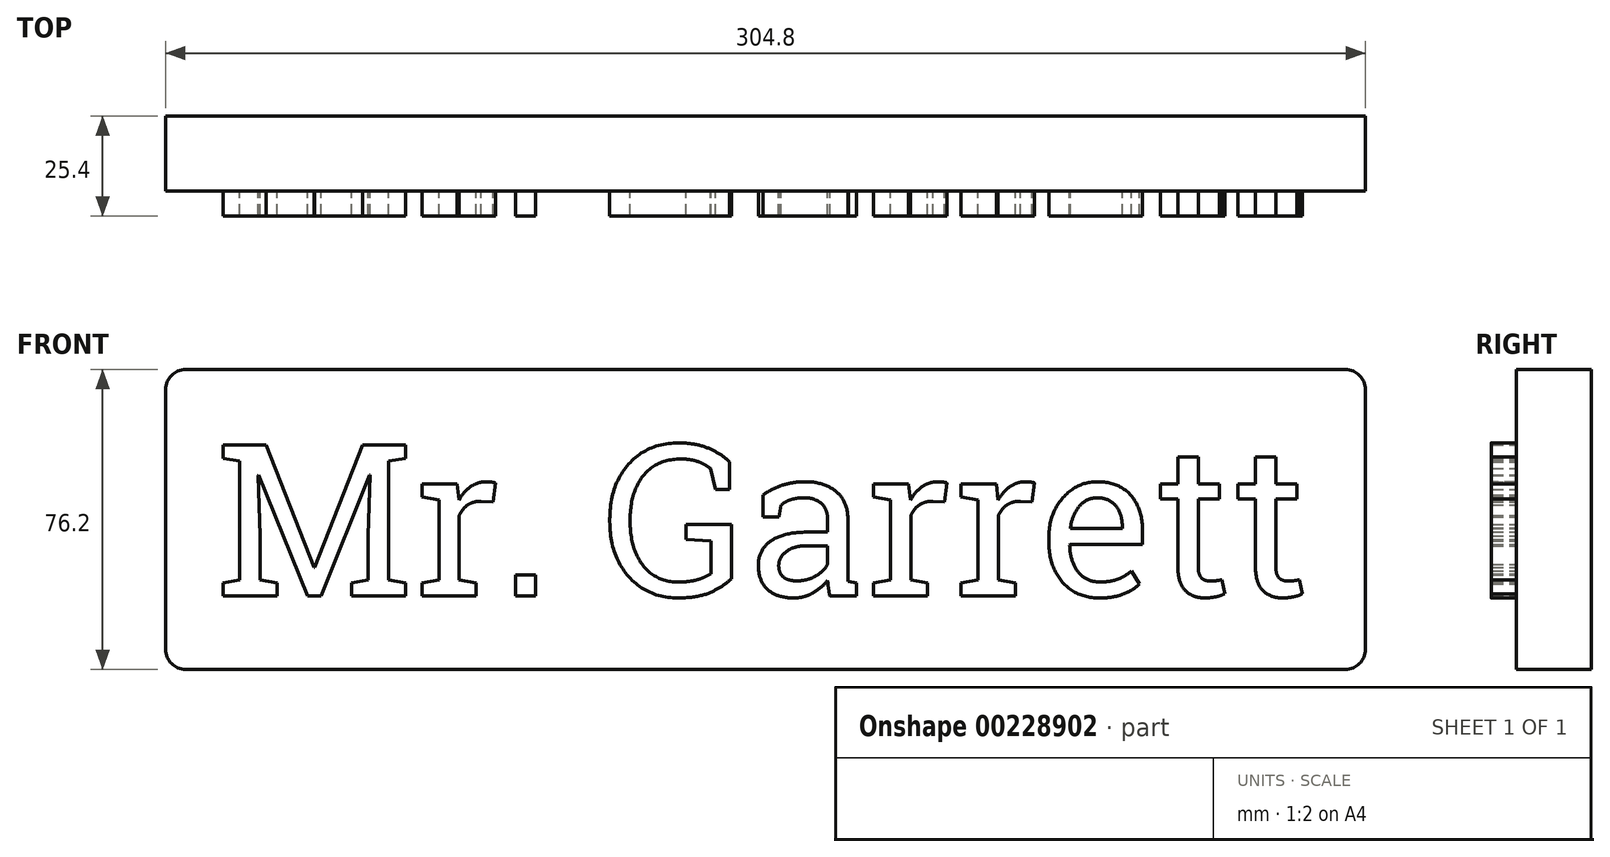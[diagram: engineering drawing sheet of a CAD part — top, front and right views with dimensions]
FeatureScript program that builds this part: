
annotation { "Feature Type Name" : "Feature", "Feature Type Description" : "" }
export const myFeature = defineFeature(function(context is Context, id is Id, definition is map)
    precondition{}
    {
        {
            var Q0;
            Q0=qCreatedBy(makeId("Front.planeOp"),FACE);
            var sketch = newSketch(context, id + "F0", { "sketchPlane" : qUnion([Q0])});
            skLineSegment(sketch, "E0.bottom", {"start": v(-152.4, 38.1) * mm, "end": v(152.4, 38.1) * mm});
            skLineSegment(sketch, "E0.top", {"start": v(-152.4, -38.1) * mm, "end": v(152.4, -38.1) * mm});
            skLineSegment(sketch, "E0.left", {"start": v(-152.4, 38.1) * mm, "end": v(-152.4, -38.1) * mm});
            skLineSegment(sketch, "E0.right", {"start": v(152.4, 38.1) * mm, "end": v(152.4, -38.1) * mm});
            skPoint(sketch, "E0.middle", {"position": v(0, 0) * mm});
            skSolve(sketch);
        }
        {
            var Q0;
            Q0=makeQuery(id+"F0.imprint","IMPRINT",FACE,{"disambiguationData":[TD([[makeQuery(id+"F0.imprint","IMPRINT",EDGE,{"derivedFrom":sQuery(id+"F0.wireOp",EDGE,"E0.bottom")}),-1.0]])]});
            extrude(context, id + "F1", {"entities" : qUnion([Q0]), "depth" : 19.05 * mm});
        }
        {
            var Q0;
            Q0=makeQuery(id+"F1.opExtrude","CAP_FACE",FACE,{"disambiguationData":[OSD([sQuery(id+"F0.wireOp",EDGE,"E0.bottom"),sQuery(id+"F0.wireOp",EDGE,"E0.top"),sQuery(id+"F0.wireOp",EDGE,"E0.left"),sQuery(id+"F0.wireOp",EDGE,"E0.right")])],"isStart":false});
            var sketch = newSketch(context, id + "F2", { "sketchPlane" : qUnion([Q0])});
            skText(sketch, "E1", { "text": "Mr. Garrett", "fontName": "RobotoSlab-Regular.ttf"});
            const initialGuessF2  = {"E1": [-0.1397, -0.01938, 1, 0, 0.03876]};
            skSetInitialGuess(sketch, initialGuessF2);
            skSolve(sketch);
        }
        {
            var Q0;
            Q0 = qSketchRegion(id + "F2", true);
            extrude(context, id + "F3", {"entities" : qUnion([Q0]), "operationType" : NewBodyOperationType.ADD, "depth" : 6.35 * mm});
        }
        {
            var Q0;
            Q0=makeQuery(id+"F1.opExtrude","SWEPT_EDGE",EDGE,{"disambiguationData":[OSD([sQuery(id+"F0.wireOp",EDGE,"E0.bottom"),sQuery(id+"F0.wireOp",EDGE,"E0.left")])]});
            var Q1;
            Q1=makeQuery(id+"F1.opExtrude","SWEPT_EDGE",EDGE,{"disambiguationData":[OSD([sQuery(id+"F0.wireOp",EDGE,"E0.bottom"),sQuery(id+"F0.wireOp",EDGE,"E0.right")])]});
            var Q2;
            Q2=makeQuery(id+"F1.opExtrude","SWEPT_EDGE",EDGE,{"disambiguationData":[OSD([sQuery(id+"F0.wireOp",EDGE,"E0.top"),sQuery(id+"F0.wireOp",EDGE,"E0.right")])]});
            var Q3;
            Q3=makeQuery(id+"F1.opExtrude","SWEPT_EDGE",EDGE,{"disambiguationData":[OSD([sQuery(id+"F0.wireOp",EDGE,"E0.top"),sQuery(id+"F0.wireOp",EDGE,"E0.left")])]});
            fillet(context, id + "F4", {"entities" : qUnion([Q0, Q1, Q2, Q3]), "radius" : 5.08 * mm, "tangentPropagation" : true, "allowEdgeOverflow" : false});
        }
    });
